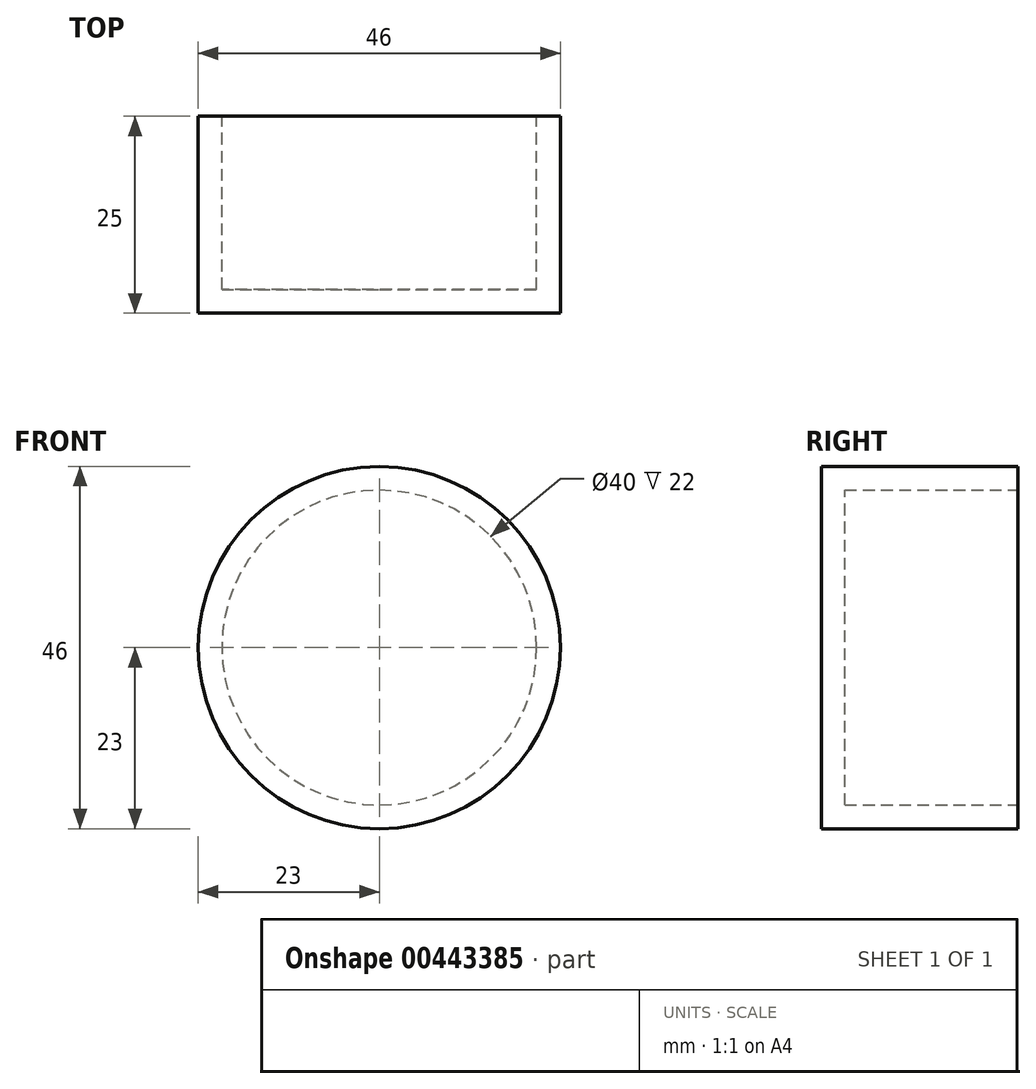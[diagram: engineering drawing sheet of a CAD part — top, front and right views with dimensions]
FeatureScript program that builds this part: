
annotation { "Feature Type Name" : "Feature", "Feature Type Description" : "" }
export const myFeature = defineFeature(function(context is Context, id is Id, definition is map)
    precondition{}
    {
        {
            var Q0;
            Q0=qCreatedBy(makeId("Front.planeOp"),FACE);
            var sketch = newSketch(context, id + "F0", { "sketchPlane" : qUnion([Q0])});
            skCircle(sketch, "E0", {"center": v(0, 0) * mm, "radius": 23 * mm});
            skCircle(sketch, "E1", {"center": v(0, 0) * mm, "radius": 20 * mm});
            skSolve(sketch);
        }
        {
            var Q0;
            Q0 = qSketchRegion(id + "F0", true);
            extrude(context, id + "F1", {"entities" : qUnion([Q0]), "depth" : 25 * mm});
        }
        {
            var Q0;
            Q0=makeQuery(id+"F1.opExtrude","CAP_FACE",FACE,{"disambiguationData":[OSD([sQuery(id+"F0.wireOp",EDGE,"E0"),sQuery(id+"F0.wireOp",EDGE,"E1")])],"isStart":false});
            var sketch = newSketch(context, id + "F2", { "sketchPlane" : qUnion([Q0])});
            skCircle(sketch, "E2", {"center": v(0, 0) * mm, "radius": 23 * mm});
            skSolve(sketch);
        }
        {
            var Q0;
            Q0 = qSketchRegion(id + "F2", true);
            extrude(context, id + "F3", {"entities" : qUnion([Q0]), "operationType" : NewBodyOperationType.ADD, "oppositeDirection" : true, "depth" : 3 * mm});
        }
    });
